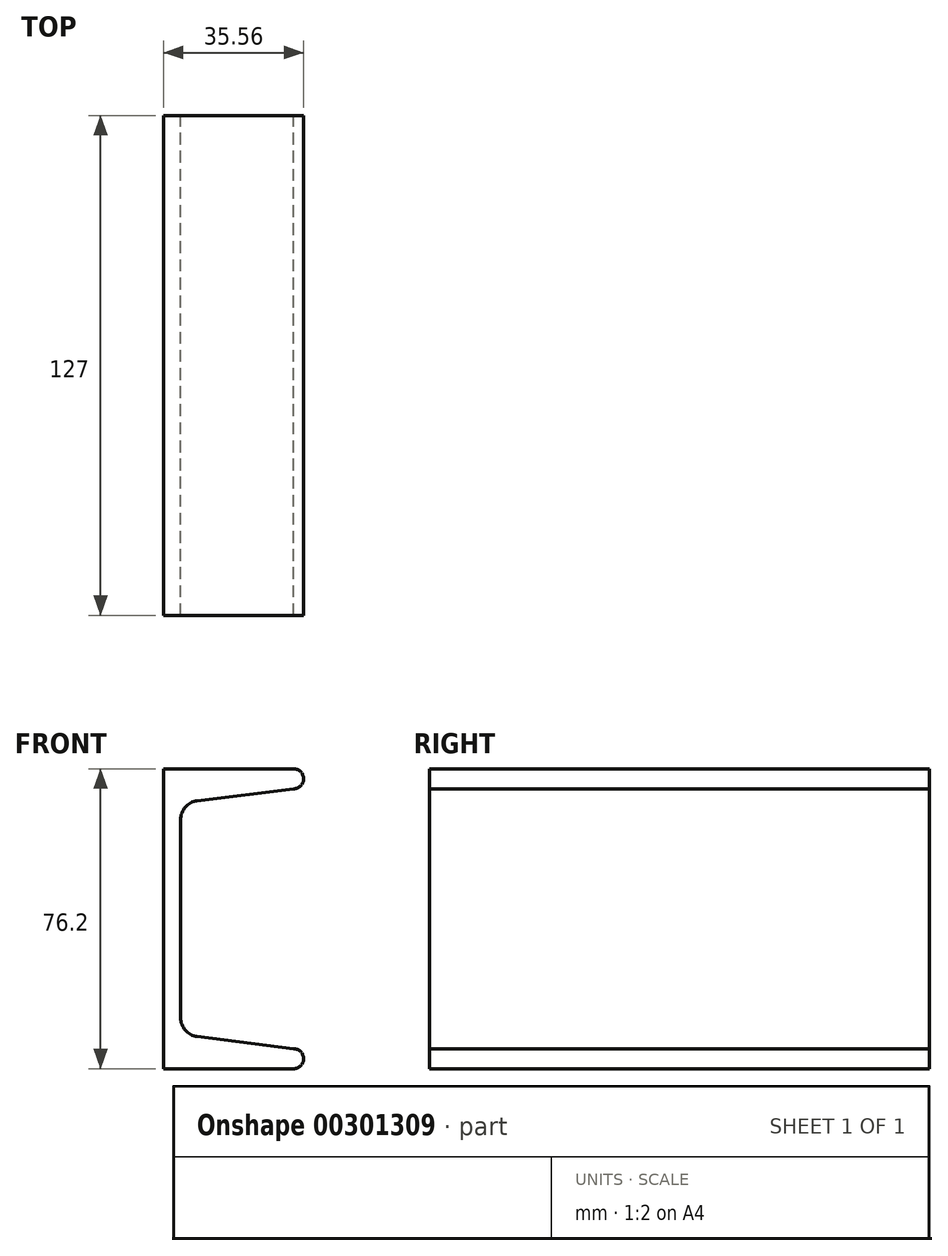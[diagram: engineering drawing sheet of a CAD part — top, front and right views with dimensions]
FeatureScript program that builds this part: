
annotation { "Feature Type Name" : "Feature", "Feature Type Description" : "" }
export const myFeature = defineFeature(function(context is Context, id is Id, definition is map)
    precondition{}
    {
        {
            var Q0;
            Q0=qCreatedBy(makeId("Front.planeOp"),FACE);
            var sketch = newSketch(context, id + "F0", { "sketchPlane" : qUnion([Q0])});
            skLineSegment(sketch, "E0", {"start": v(-43.32, 38.1) * mm, "end": v(-43.32, 0) * mm});
            skLineSegment(sketch, "E1", {"start": v(-43.32, 38.1) * mm, "end": v(-10.3, 38.1) * mm});
            skArc(sketch, "E2", {"start": v(-10.3, 33.02) * mm, "mid": v(-7.76, 35.56) * mm, "end": v(-10.3, 38.1) * mm});
            skLineSegment(sketch, "E3", {"start": v(-10.3, 33.02) * mm, "end": v(-34.75, 29.95) * mm});
            skLineSegment(sketch, "E4", {"start": v(-39, 25.14) * mm, "end": v(-39, 0) * mm});
            skPoint(sketch, "E5.visualSharp", {"position": v(-39, 29.42) * mm});
            skArc(sketch, "E5.filletArc", {"start": v(-34.75, 29.95) * mm, "mid": v(-37.79, 28.35) * mm, "end": v(-39, 25.14) * mm});
            skLineSegment(sketch, "E6", {"start": v(21.78, 38.1) * mm, "end": v(23.04, 38.1) * mm});
            skArc(sketch, "E7.MirrorCS", {"start": v(-10.3, -33.02) * mm, "mid": v(-7.76, -35.56) * mm, "end": v(-10.3, -38.1) * mm});
            skArc(sketch, "E8.MirrorCS", {"start": v(-34.75, -29.95) * mm, "mid": v(-37.79, -28.35) * mm, "end": v(-39, -25.14) * mm});
            skLineSegment(sketch, "E9.MirrorCS", {"start": v(-43.32, -38.1) * mm, "end": v(-43.32, 0) * mm});
            skLineSegment(sketch, "E10.MirrorCS", {"start": v(-10.3, -33.02) * mm, "end": v(-34.75, -29.95) * mm});
            skLineSegment(sketch, "E11.MirrorCS", {"start": v(-39, -25.14) * mm, "end": v(-39, 0) * mm});
            skLineSegment(sketch, "E12.MirrorCS", {"start": v(-43.32, -38.1) * mm, "end": v(-10.3, -38.1) * mm});
            skPoint(sketch, "E13.MirrorP", {"position": v(-39, -29.42) * mm});
            skSolve(sketch);
        }
        {
            var Q0;
            Q0=makeQuery(id+"F0.imprint","IMPRINT",FACE,{"disambiguationData":[TD([[makeQuery(id+"F0.imprint","IMPRINT",EDGE,{"derivedFrom":sQuery(id+"F0.wireOp",EDGE,"E0")}),1.0]])]});
            extrude(context, id + "F1", {"entities" : qUnion([Q0]), "endBound" : BoundingType.SYMMETRIC, "depth" : 127 * mm});
        }
    });
